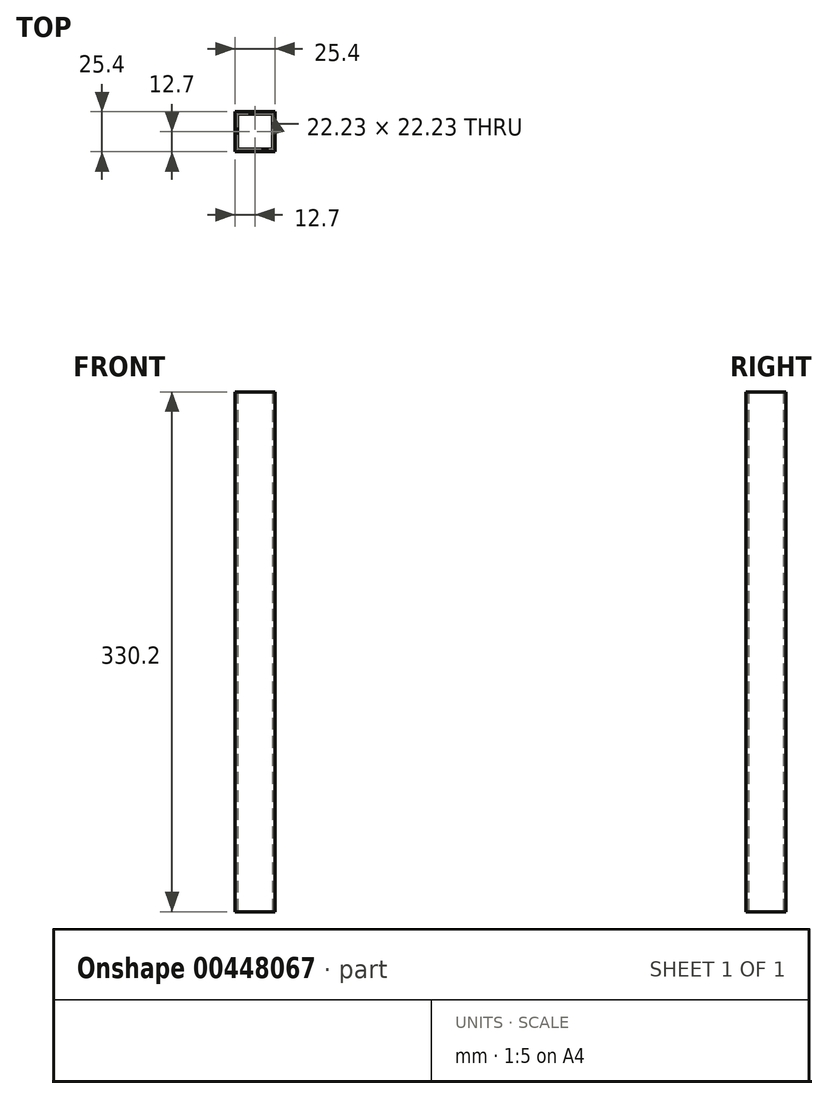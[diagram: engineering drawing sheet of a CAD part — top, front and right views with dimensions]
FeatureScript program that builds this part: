
annotation { "Feature Type Name" : "Feature", "Feature Type Description" : "" }
export const myFeature = defineFeature(function(context is Context, id is Id, definition is map)
    precondition{}
    {
        {
            var Q0;
            Q0=qCreatedBy(makeId("Top.planeOp"),FACE);
            var sketch = newSketch(context, id + "F0", { "sketchPlane" : qUnion([Q0])});
            skLineSegment(sketch, "E0.bottom", {"start": v(-12.7, 12.7) * mm, "end": v(12.7, 12.7) * mm});
            skLineSegment(sketch, "E0.top", {"start": v(-12.7, -12.7) * mm, "end": v(12.7, -12.7) * mm});
            skLineSegment(sketch, "E0.left", {"start": v(-12.7, 12.7) * mm, "end": v(-12.7, -12.7) * mm});
            skLineSegment(sketch, "E0.right", {"start": v(12.7, 12.7) * mm, "end": v(12.7, -12.7) * mm});
            skPoint(sketch, "E0.middle", {"position": v(0, 0) * mm});
            skSolve(sketch);
        }
        {
            var Q0;
            Q0 = qSketchRegion(id + "F0", true);
            extrude(context, id + "F1", {"entities" : qUnion([Q0]), "depth" : 330.2 * mm});
        }
        {
            var Q0;
            Q0=makeQuery(id+"F1.opExtrude","CAP_FACE",FACE,{"disambiguationData":[OSD([sQuery(id+"F0.wireOp",EDGE,"E0.bottom"),sQuery(id+"F0.wireOp",EDGE,"E0.top"),sQuery(id+"F0.wireOp",EDGE,"E0.left"),sQuery(id+"F0.wireOp",EDGE,"E0.right")])],"isStart":false});
            var Q1;
            Q1=makeQuery(id+"F1.opExtrude","SWEPT_BODY",BODY,{"disambiguationData":[OSD([sQuery(id+"F0.wireOp",EDGE,"E0.bottom"),sQuery(id+"F0.wireOp",EDGE,"E0.top"),sQuery(id+"F0.wireOp",EDGE,"E0.left"),sQuery(id+"F0.wireOp",EDGE,"E0.right")])]});
            shell(context, id + "F2", {"entities" : qUnion([Q0]), "parts" : qUnion([Q1]), "thickness" : 1.59 * mm});
        }
        {
            var Q0;
            Q0=makeQuery(id+"F2.opShell","OFFSET_FACE",FACE,{"disambiguationData":[OSD([sQuery(id+"F0.wireOp",EDGE,"E0.bottom"),sQuery(id+"F0.wireOp",EDGE,"E0.top"),sQuery(id+"F0.wireOp",EDGE,"E0.left"),sQuery(id+"F0.wireOp",EDGE,"E0.right")])]});
            extrude(context, id + "F3", {"entities" : qUnion([Q0]), "operationType" : NewBodyOperationType.REMOVE, "oppositeDirection" : true, "depth" : 25.4 * mm});
        }
    });
